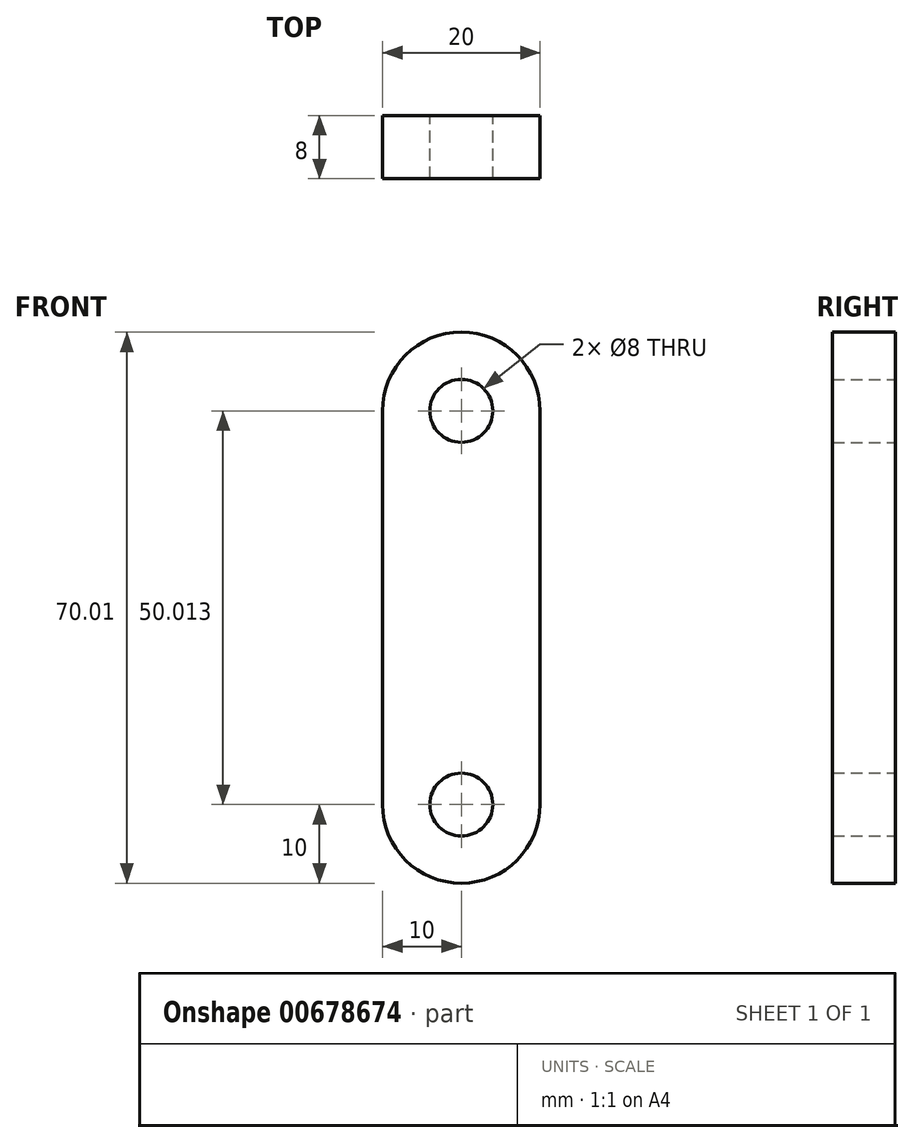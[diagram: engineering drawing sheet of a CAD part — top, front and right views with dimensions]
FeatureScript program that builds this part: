
annotation { "Feature Type Name" : "Feature", "Feature Type Description" : "" }
export const myFeature = defineFeature(function(context is Context, id is Id, definition is map)
    precondition{}
    {
        {
            var Q0;
            Q0=qCreatedBy(makeId("Front.planeOp"),FACE);
            var sketch = newSketch(context, id + "F0", { "sketchPlane" : qUnion([Q0])});
            skArc(sketch, "E0", {"start": v(10, 50.01) * mm, "mid": v(0, 60.01) * mm, "end": v(-10, 50.01) * mm});
            skCircle(sketch, "E1", {"center": v(0, 50.01) * mm, "radius": 4 * mm});
            skArc(sketch, "E2", {"start": v(-10, 0) * mm, "mid": v(0, -10) * mm, "end": v(10, 0) * mm});
            skCircle(sketch, "E3", {"center": v(0, 0) * mm, "radius": 4 * mm});
            skLineSegment(sketch, "E4", {"start": v(10, 50.01) * mm, "end": v(10, 0) * mm});
            skLineSegment(sketch, "E5", {"start": v(-10, 0) * mm, "end": v(-10, 50.01) * mm});
            skSolve(sketch);
        }
        {
            var Q0;
            Q0 = qSketchRegion(id + "F0", true);
            extrude(context, id + "F1", {"entities" : qUnion([Q0]), "depth" : 8 * mm, "offsetDistance" : 25.4 * mm});
        }
    });
